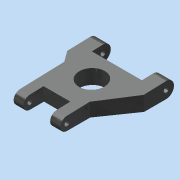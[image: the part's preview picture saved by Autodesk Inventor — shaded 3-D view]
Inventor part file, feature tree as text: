
AUTODESK INVENTOR PART (.ipt)
format: ipt  version: 2013 (Build 170138000, 138)  size: 148,992 bytes
history: native  units: in
note: dims shown in document units (in); Inventor stores cm internally (conversion verified against a paired STEP export)
features: extrude x2, plane x2, sketch x2
ambient origin geometry x8: Origin, YZ Plane, XZ Plane, XY Plane, X Axis, Y Axis, Z Axis, Center Point
bodies: Solid1 (feature_tree)
feature tree (6):
  extrude  "Extrusion1"  Depth=0.115in
  extrude  "Extrusion2"  Depth=0.115in
  plane  "Work Plane1"
  plane  "Work Plane2"
  sketch  "Sketch2"  dims[d0=0.31in d1=0.115in]
  sketch  "Sketch3"  dims[d2=0.37in d3=0.115in d4=2.16in d5=1.8in d6=0.0in d10=0.23in d12=0.63in d14=1.2in d16=0.31in d17=0.44in d18=0.48in d19=0.0in d20=0.0in d21=1.45in d22=0.24in d24=0.7in d25=0.61in d26=0.24in d27=0.37in d28=1.18in d29=0.18in]
